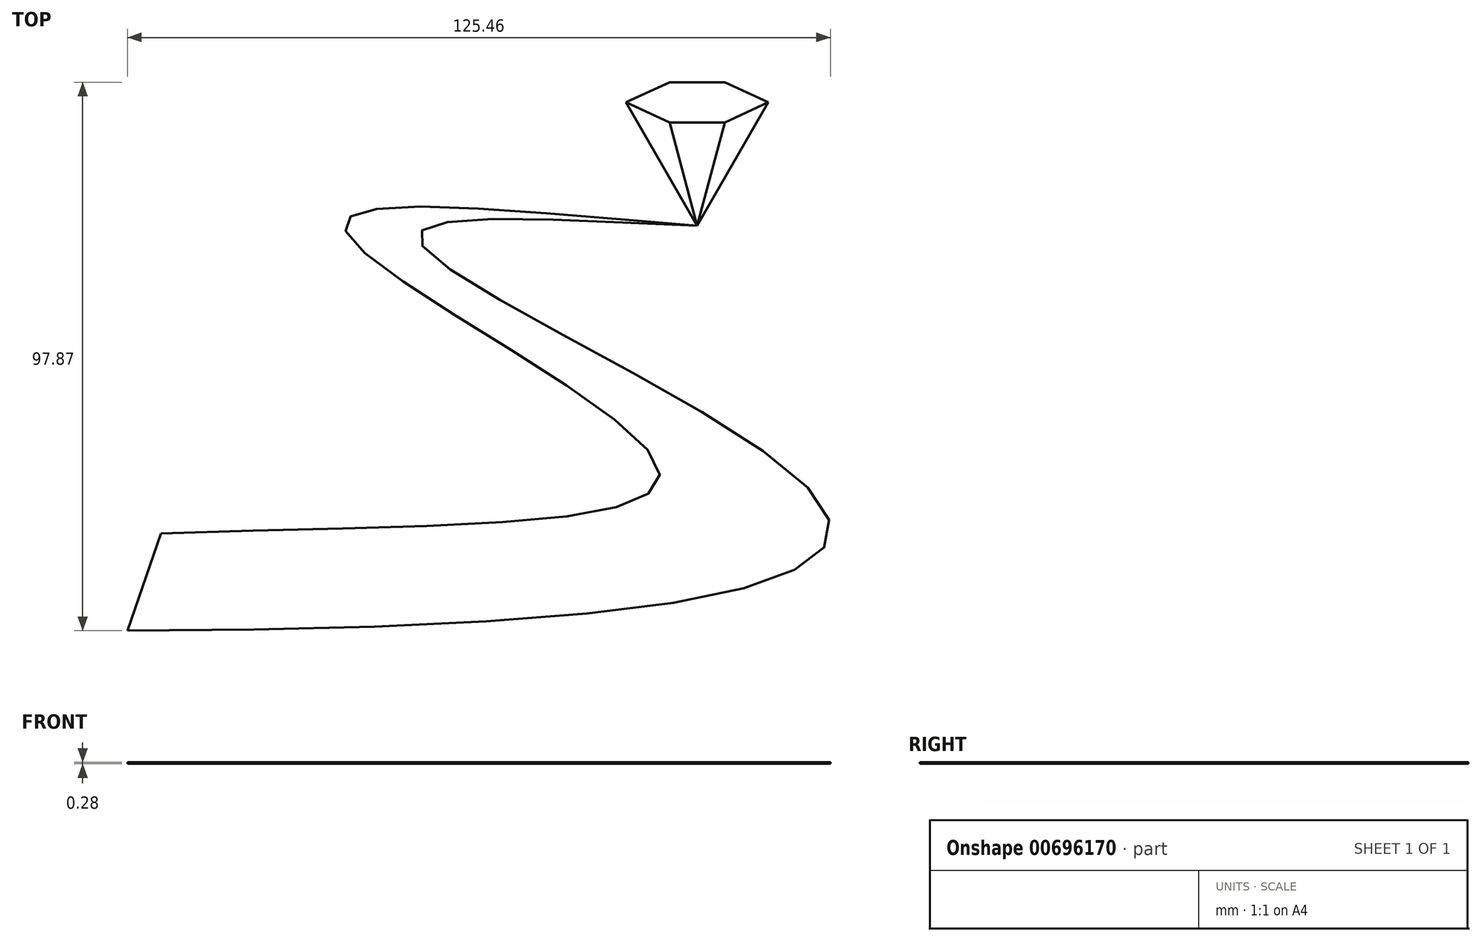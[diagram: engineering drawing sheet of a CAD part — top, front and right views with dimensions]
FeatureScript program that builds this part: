
annotation { "Feature Type Name" : "Feature", "Feature Type Description" : "" }
export const myFeature = defineFeature(function(context is Context, id is Id, definition is map)
    precondition{}
    {
        {
            var Q0;
            Q0=qCreatedBy(makeId("Top.planeOp"),FACE);
            var sketch = newSketch(context, id + "F0", { "sketchPlane" : qUnion([Q0])});
            skFitSpline(sketch, "E0", {"points": [v(32.33, 30.53) * mm, v(-30.3, 29.27) * mm, v(25.18, -12.02) * mm, v(-63.4, -24.43) * mm], "startDerivative": vector(-314.81, 24.44) * mm, "endDerivative": vector(-378.98, -14.7) * mm});
            skFitSpline(sketch, "E1", {"points": [v(32.33, 30.53) * mm, v(-17.03, 27.34) * mm, v(54.98, -19.91) * mm, v(-69.37, -41.75) * mm], "startDerivative": vector(-307.28, 10.48) * mm, "endDerivative": vector(-527.68, -0.78) * mm});
            skLineSegment(sketch, "E2", {"start": v(-63.4, -24.43) * mm, "end": v(-69.37, -41.75) * mm});
            skSolve(sketch);
        }
        {
            var Q0;
            Q0 = qSketchRegion(id + "F0", true);
            extrude(context, id + "F1", {"entities" : qUnion([Q0]), "depth" : 0.25 * mm, "offsetDistance" : 25.4 * mm});
        }
        {
            var Q0;
            Q0=qCreatedBy(makeId("Top.planeOp"),FACE);
            var sketch = newSketch(context, id + "F2", { "sketchPlane" : qUnion([Q0])});
            skPoint(sketch, "E3", {"position": v(32.33, 30.53) * mm});
            skLineSegment(sketch, "E4", {"start": v(32.33, 30.53) * mm, "end": v(45.03, 52.52) * mm});
            skLineSegment(sketch, "E5", {"start": v(32.33, 30.53) * mm, "end": v(19.63, 52.52) * mm, "construction": true});
            skLineSegment(sketch, "E6", {"start": v(32.33, 30.53) * mm, "end": v(27.4, 48.93) * mm});
            skLineSegment(sketch, "E7", {"start": v(27.4, 48.93) * mm, "end": v(37.26, 48.93) * mm});
            skLineSegment(sketch, "E8", {"start": v(37.26, 48.93) * mm, "end": v(45.03, 52.52) * mm});
            skLineSegment(sketch, "E9", {"start": v(37.26, 48.93) * mm, "end": v(32.33, 30.53) * mm, "construction": true});
            skSolve(sketch);
        }
        {
            var Q0;
            Q0 = qSketchRegion(id + "F2", true);
            extrude(context, id + "F3", {"entities" : qUnion([Q0]), "depth" : 0.25 * mm, "offsetDistance" : 25.4 * mm});
        }
        {
            var Q0;
            Q0=qCreatedBy(makeId("Top.planeOp"),FACE);
            var sketch = newSketch(context, id + "F4", { "sketchPlane" : qUnion([Q0])});
            skLineSegment(sketch, "E10", {"start": v(19.63, 52.52) * mm, "end": v(32.33, 30.53) * mm});
            skLineSegment(sketch, "E11", {"start": v(19.63, 52.52) * mm, "end": v(27.4, 48.93) * mm});
            skLineSegment(sketch, "E12", {"start": v(27.4, 48.93) * mm, "end": v(32.33, 30.53) * mm});
            skSolve(sketch);
        }
        {
            var Q0;
            Q0 = qSketchRegion(id + "F4", true);
            extrude(context, id + "F5", {"entities" : qUnion([Q0]), "depth" : 0.25 * mm, "offsetDistance" : 25.4 * mm});
        }
        {
            var Q0;
            Q0=qCreatedBy(makeId("Top.planeOp"),FACE);
            var sketch = newSketch(context, id + "F6", { "sketchPlane" : qUnion([Q0])});
            skLineSegment(sketch, "E13", {"start": v(19.63, 52.52) * mm, "end": v(27.4, 48.93) * mm});
            skLineSegment(sketch, "E14", {"start": v(27.4, 48.93) * mm, "end": v(37.26, 48.93) * mm});
            skLineSegment(sketch, "E15", {"start": v(37.26, 48.93) * mm, "end": v(45.03, 52.52) * mm});
            skLineSegment(sketch, "E16", {"start": v(45.03, 52.52) * mm, "end": v(37.26, 56.12) * mm});
            skLineSegment(sketch, "E17", {"start": v(37.26, 56.12) * mm, "end": v(27.4, 56.12) * mm});
            skLineSegment(sketch, "E18", {"start": v(27.4, 56.12) * mm, "end": v(19.63, 52.52) * mm});
            skSolve(sketch);
        }
        {
            var Q0;
            Q0 = qSketchRegion(id + "F6", true);
            extrude(context, id + "F7", {"entities" : qUnion([Q0]), "depth" : 0.25 * mm, "offsetDistance" : 25.4 * mm});
        }
        {
            var Q0;
            Q0=makeQuery(id+"F3.opExtrude","CAP_FACE",FACE,{"disambiguationData":[OSD([sQuery(id+"F2.wireOp",EDGE,"E4"),sQuery(id+"F2.wireOp",EDGE,"E6"),sQuery(id+"F2.wireOp",EDGE,"E7"),sQuery(id+"F2.wireOp",EDGE,"E8")])],"isStart":false});
            var sketch = newSketch(context, id + "F8", { "sketchPlane" : qUnion([Q0])});
            skLineSegment(sketch, "E19", {"start": v(37.26, 48.93) * mm, "end": v(32.33, 30.53) * mm});
            skLineSegment(sketch, "E20", {"start": v(32.33, 30.53) * mm, "end": v(45.03, 52.52) * mm});
            skLineSegment(sketch, "E21", {"start": v(45.03, 52.52) * mm, "end": v(37.26, 48.93) * mm});
            skSolve(sketch);
        }
        {
            var Q0;
            Q0 = qSketchRegion(id + "F8", true);
            extrude(context, id + "F9", {"entities" : qUnion([Q0]), "depth" : 0.03 * mm, "offsetDistance" : 25.4 * mm});
        }
    });
